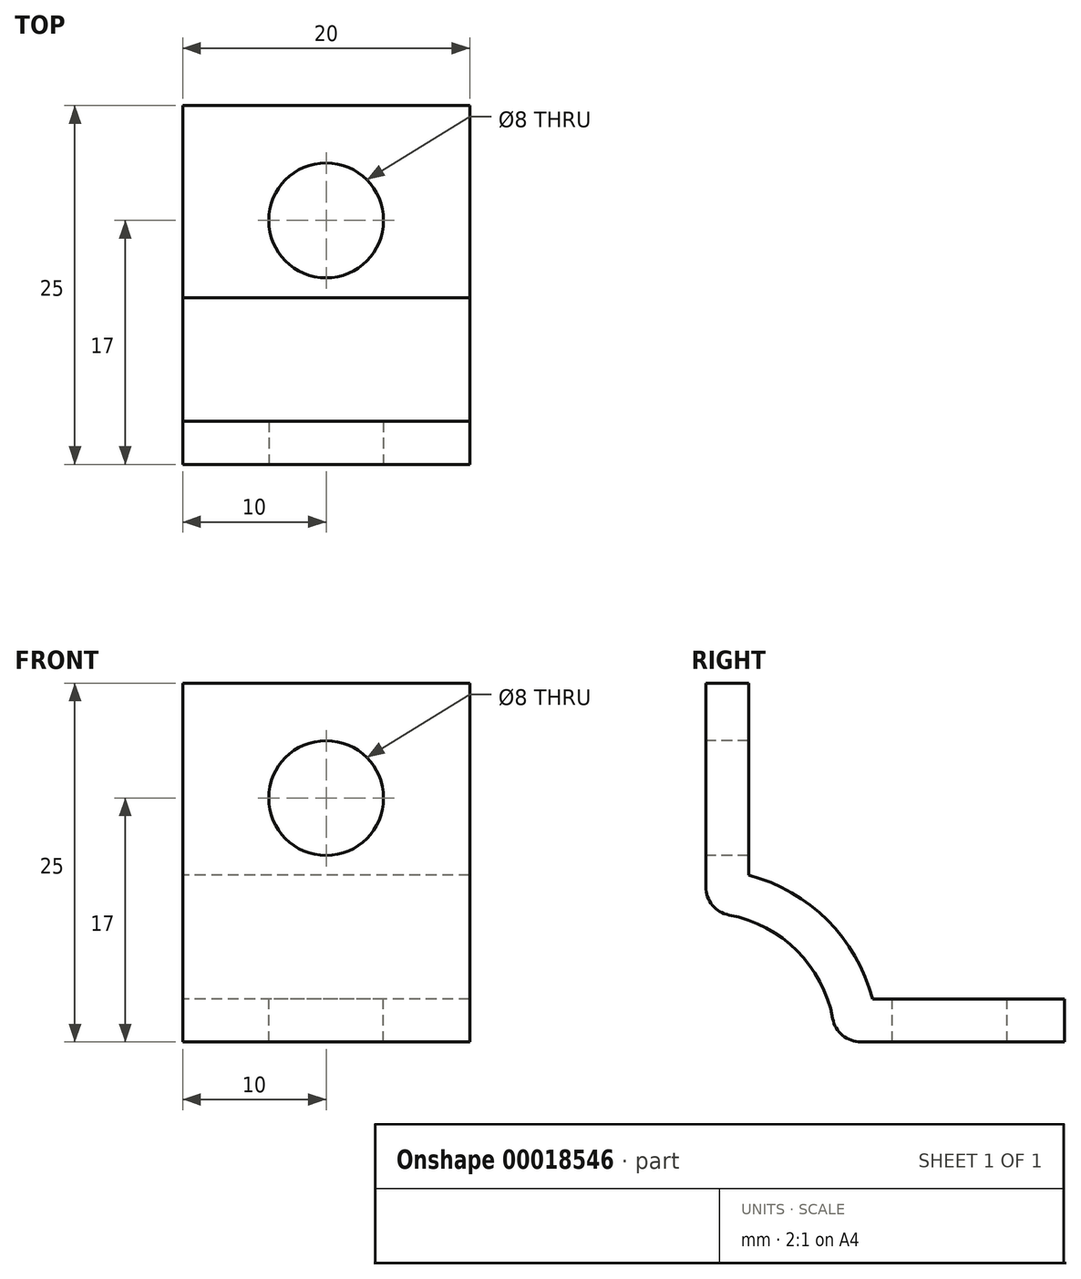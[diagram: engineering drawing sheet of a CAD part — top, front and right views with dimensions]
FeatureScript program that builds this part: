
annotation { "Feature Type Name" : "Feature", "Feature Type Description" : "" }
export const myFeature = defineFeature(function(context is Context, id is Id, definition is map)
    precondition{}
    {
        {
            var Q0;
            Q0=qCreatedBy(makeId("Right.planeOp"),FACE);
            var sketch = newSketch(context, id + "F0", { "sketchPlane" : qUnion([Q0])});
            skCircle(sketch, "E0", {"center": v(0, 0) * mm, "radius": 9 * mm});
            skLineSegment(sketch, "E1.bottom", {"start": v(0, 0) * mm, "end": v(25, 0) * mm});
            skLineSegment(sketch, "E1.top", {"start": v(0, 3) * mm, "end": v(25, 3) * mm});
            skLineSegment(sketch, "E1.left", {"start": v(0, 0) * mm, "end": v(0, 3) * mm});
            skLineSegment(sketch, "E1.right", {"start": v(25, 0) * mm, "end": v(25, 3) * mm});
            skLineSegment(sketch, "E2.bottom", {"start": v(0, 0) * mm, "end": v(3, 0) * mm});
            skLineSegment(sketch, "E2.top", {"start": v(0, 25) * mm, "end": v(3, 25) * mm});
            skLineSegment(sketch, "E2.left", {"start": v(0, 0) * mm, "end": v(0, 25) * mm});
            skLineSegment(sketch, "E2.right", {"start": v(3, 0) * mm, "end": v(3, 25) * mm});
            skCircle(sketch, "E3", {"center": v(0, 0) * mm, "radius": 12 * mm});
            skSolve(sketch);
        }
        {
            var Q0;
            {var subQ5=sQuery(id+"F0.wireOp",EDGE,"E2.top");Q0=makeQuery(id+"F0.imprint","IMPRINT",FACE,{"disambiguationData":[TD([[makeQuery(id+"F0.imprint","IMPRINT",EDGE,{"derivedFrom":subQ5}),-1.0]])]});}
            var Q1;
            {var subQ5=sQuery(id+"F0.wireOp",EDGE,"E1.right");Q1=makeQuery(id+"F0.imprint","IMPRINT",FACE,{"disambiguationData":[TD([[makeQuery(id+"F0.imprint","IMPRINT",EDGE,{"derivedFrom":subQ5}),1.0]])]});}
            var Q2;
            {var subQ1=sQuery(id+"F0.wireOp",EDGE,"E2.right");var subQ5=sQuery(id+"F0.wireOp",EDGE,"E0");var subQ6=makeQuery(id+"F0.imprint","INTERSECT",VERTEX,{"derivedFrom":[subQ5,subQ1]});Q2=makeQuery(id+"F0.imprint","IMPRINT",FACE,{"disambiguationData":[TD([[makeQuery(id+"F0.imprint","IMPRINT",EDGE,{"disambiguationData":[TD([[subQ6,-1.0]])],"derivedFrom":subQ5}),-1.0]])]});}
            var Q3;
            {var subQ3=sQuery(id+"F0.wireOp",EDGE,"E1.top");var subQ5=sQuery(id+"F0.wireOp",EDGE,"E0");var subQ7=makeQuery(id+"F0.imprint","INTERSECT",VERTEX,{"derivedFrom":[subQ5,subQ3]});Q3=makeQuery(id+"F0.imprint","IMPRINT",FACE,{"disambiguationData":[TD([[makeQuery(id+"F0.imprint","IMPRINT",EDGE,{"disambiguationData":[TD([[subQ7,-1.0]])],"derivedFrom":subQ5}),-1.0]])]});}
            var Q4;
            {var subQ1=sQuery(id+"F0.wireOp",EDGE,"E1.top");var subQ5=sQuery(id+"F0.wireOp",EDGE,"E0");var subQ6=makeQuery(id+"F0.imprint","INTERSECT",VERTEX,{"derivedFrom":[subQ5,subQ1]});Q4=makeQuery(id+"F0.imprint","IMPRINT",FACE,{"disambiguationData":[TD([[makeQuery(id+"F0.imprint","IMPRINT",EDGE,{"disambiguationData":[TD([[subQ6,1.0]])],"derivedFrom":subQ5}),-1.0]])]});}
            extrude(context, id + "F6", {"entities" : qUnion([Q0, Q1, Q2, Q3, Q4]), "depth" : 20 * mm});
        }
        {
            var Q0;
            Q0=makeQuery(id+"F6.opExtrude","SWEPT_FACE",FACE,{"disambiguationData":[OSD([sQuery(id+"F0.wireOp",EDGE,"E1.top")])]});
            var sketch = newSketch(context, id + "F1", { "sketchPlane" : qUnion([Q0])});
            skLineSegment(sketch, "E4", {"start": v(0, 17) * mm, "end": v(20, 17) * mm, "construction": true});
            skCircle(sketch, "E5", {"center": v(10, 17) * mm, "radius": 4 * mm});
            skSolve(sketch);
        }
        {
            var Q0;
            Q0=makeQuery(id+"F1.imprint","IMPRINT",FACE,{"disambiguationData":[TD([[makeQuery(id+"F1.imprint","IMPRINT",EDGE,{"derivedFrom":sQuery(id+"F1.wireOp",EDGE,"E5")}),1.0]])]});
            extrude(context, id + "F2", {"entities" : qUnion([Q0]), "oppositeDirection" : true, "depth" : 25 * mm});
        }
        {
            var Q0;
            Q0=qCreatedBy(makeId("Front.planeOp"),FACE);
            var sketch = newSketch(context, id + "F3", { "sketchPlane" : qUnion([Q0])});
            skLineSegment(sketch, "E6", {"start": v(32.93, 0) * mm, "end": v(-18.62, 0) * mm, "construction": true});
            skSolve(sketch);
        }
        {
            var Q0;
            Q0=makeQuery(id+"F2.opExtrude","SWEPT_BODY",BODY,{"disambiguationData":[OSD([sQuery(id+"F1.wireOp",EDGE,"E5")])]});
            var Q1;
            Q1=sQuery(id+"F3.wireOp",EDGE,"E6");
            circularPattern(context, id + "F4", {"operationType" : NewBodyOperationType.REMOVE, "entities" : qUnion([Q0]), "axis" : qUnion([Q1]), "angle" : 90 * degree, "instanceCount" : 2, "oppositeDirection" : true});
        }
        {
            var Q0;
            Q0=makeQuery(id+"F6.opExtrude","SWEPT_EDGE",EDGE,{"disambiguationData":[OSD([sQuery(id+"F0.wireOp",EDGE,"E0"),sQuery(id+"F0.wireOp",EDGE,"E1.bottom")])]});
            var Q1;
            Q1=makeQuery(id+"F6.opExtrude","SWEPT_EDGE",EDGE,{"disambiguationData":[OSD([sQuery(id+"F0.wireOp",EDGE,"E0"),sQuery(id+"F0.wireOp",EDGE,"E2.left")])]});
            fillet(context, id + "F5", {"entities" : qUnion([Q0, Q1]), "radius" : 2 * mm, "tangentPropagation" : true, "allowEdgeOverflow" : false});
        }
    });
